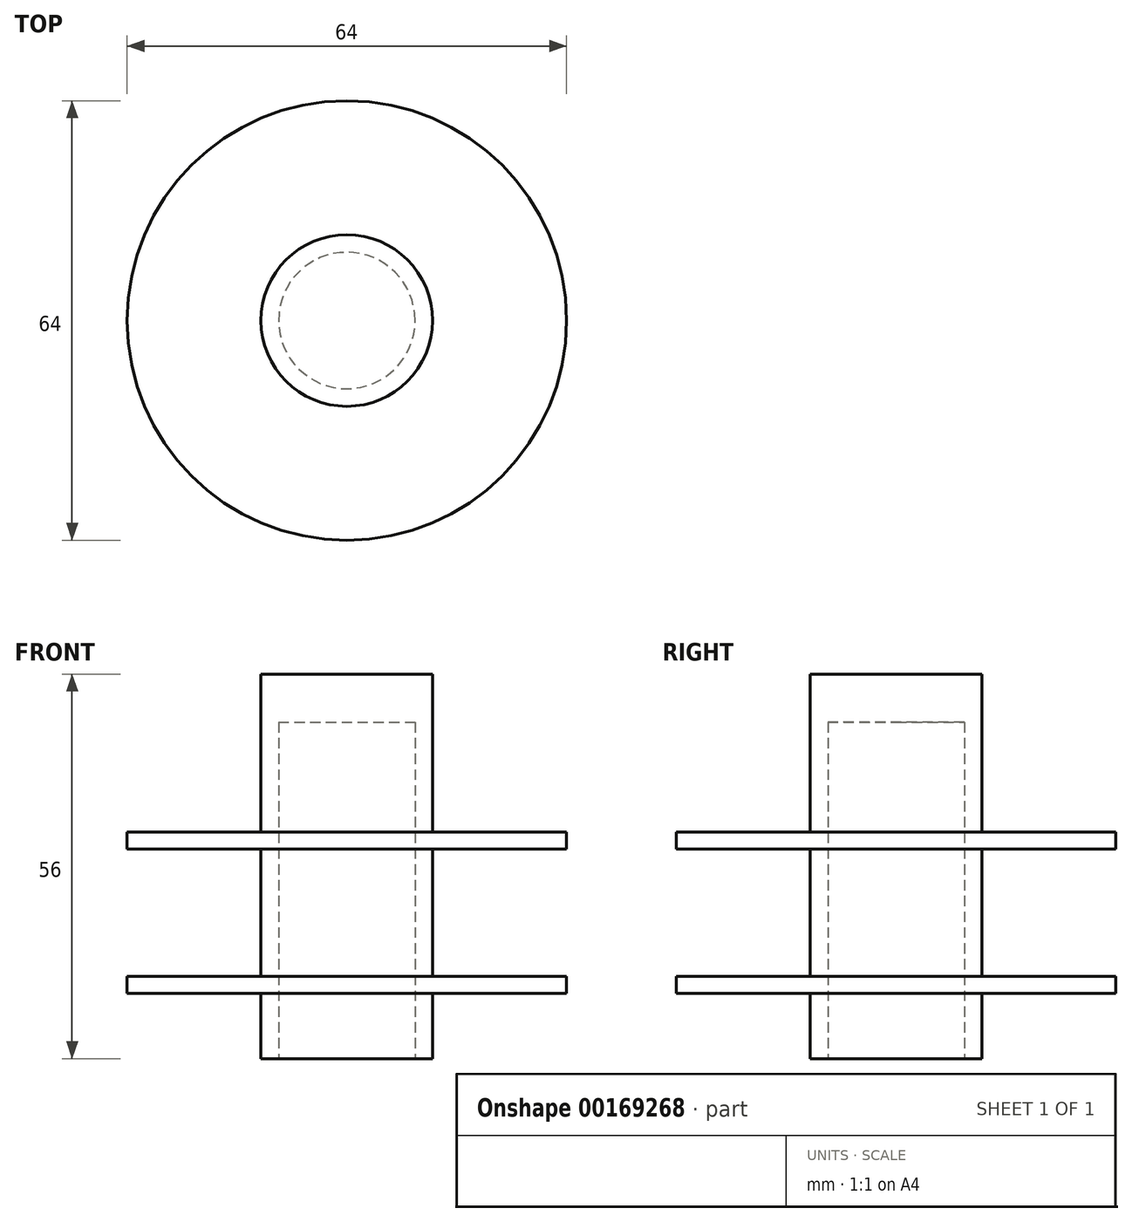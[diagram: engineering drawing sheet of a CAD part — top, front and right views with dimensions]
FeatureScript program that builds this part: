
annotation { "Feature Type Name" : "Feature", "Feature Type Description" : "" }
export const myFeature = defineFeature(function(context is Context, id is Id, definition is map)
    precondition{}
    {
        {
            var Q0;
            Q0=qCreatedBy(makeId("Front.planeOp"),FACE);
            var sketch = newSketch(context, id + "F0", { "sketchPlane" : qUnion([Q0])});
            skLineSegment(sketch, "E0", {"start": v(12.5, 25.5) * mm, "end": v(12.5, 2.5) * mm});
            skLineSegment(sketch, "E1", {"start": v(12.5, 2.5) * mm, "end": v(32, 2.5) * mm});
            skLineSegment(sketch, "E2", {"start": v(32, 2.5) * mm, "end": v(32, 0) * mm});
            skLineSegment(sketch, "E3", {"start": v(32, 0) * mm, "end": v(12.5, 0) * mm});
            skLineSegment(sketch, "E4", {"start": v(12.5, 0) * mm, "end": v(12.5, -18.5) * mm});
            skLineSegment(sketch, "E5", {"start": v(12.5, -18.5) * mm, "end": v(32, -18.5) * mm});
            skLineSegment(sketch, "E6", {"start": v(32, -18.5) * mm, "end": v(32, -21) * mm});
            skLineSegment(sketch, "E7", {"start": v(32, -21) * mm, "end": v(12.5, -21) * mm});
            skLineSegment(sketch, "E8", {"start": v(12.5, -21) * mm, "end": v(12.5, -30.5) * mm});
            skLineSegment(sketch, "E9", {"start": v(12.5, 25.5) * mm, "end": v(0, 25.5) * mm});
            skLineSegment(sketch, "E10", {"start": v(0, 25.5) * mm, "end": v(0, 18.5) * mm});
            skLineSegment(sketch, "E11", {"start": v(0, 18.5) * mm, "end": v(9.94, 18.5) * mm});
            skLineSegment(sketch, "E12", {"start": v(9.94, 18.5) * mm, "end": v(9.94, -30.5) * mm});
            skLineSegment(sketch, "E13", {"start": v(9.94, -30.5) * mm, "end": v(12.5, -30.5) * mm});
            skSolve(sketch);
        }
        {
            var Q0;
            Q0 = qSketchRegion(id + "F0", true);
            var Q1;
            Q1=sQuery(id+"F0.wireOp",EDGE,"E10");
            revolve(context, id + "F1", {"entities" : qUnion([Q0]), "axis" : qUnion([Q1]), "revolveType" : RevolveType.FULL, "oppositeDirection" : true});
        }
    });
